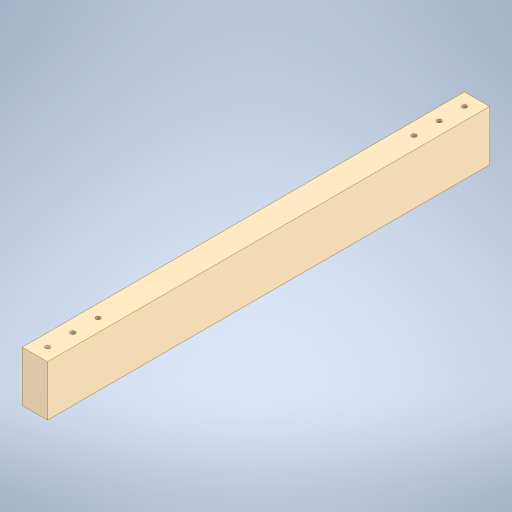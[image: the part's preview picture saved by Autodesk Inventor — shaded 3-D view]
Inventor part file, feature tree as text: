
AUTODESK INVENTOR PART (.ipt)
format: ipt  version: 2023.4 (Build 274418000, 418)  size: 242,688 bytes
history: native  units: in
note: dims shown in document units (in); Inventor stores cm internally (conversion verified against a paired STEP export)
features: extrude x3, sketch x3
ambient origin geometry x8: Origin, YZ Plane, XZ Plane, XY Plane, X Axis, Y Axis, Z Axis, Center Point
bodies: Body1 (feature_tree)
feature tree (6):
  extrude  "Extrusion2"  Depth=2.0in
  extrude  "Extrusion3"  Depth=17.5in
  extrude  "Extrusion4"  Depth=1.0in
  sketch  "Sketch2"  dims[d4=1.0in d5=2.0in]
  sketch  "Sketch3"  dims[d6=17.5in d7=0.0in d8=0.177in]
  sketch  "Sketch4"  dims[d9=0.5in d10=0.5in d11=1.1811in d13=1.0in d14=0.3937in d16=1.0in d18=24.0in d19=0.0in d20=0.177in d21=0.5in d22=0.5in d23=1.1811in d25=1.0in d26=0.3937in d28=1.0in d30=24.0in d31=0.0in]
